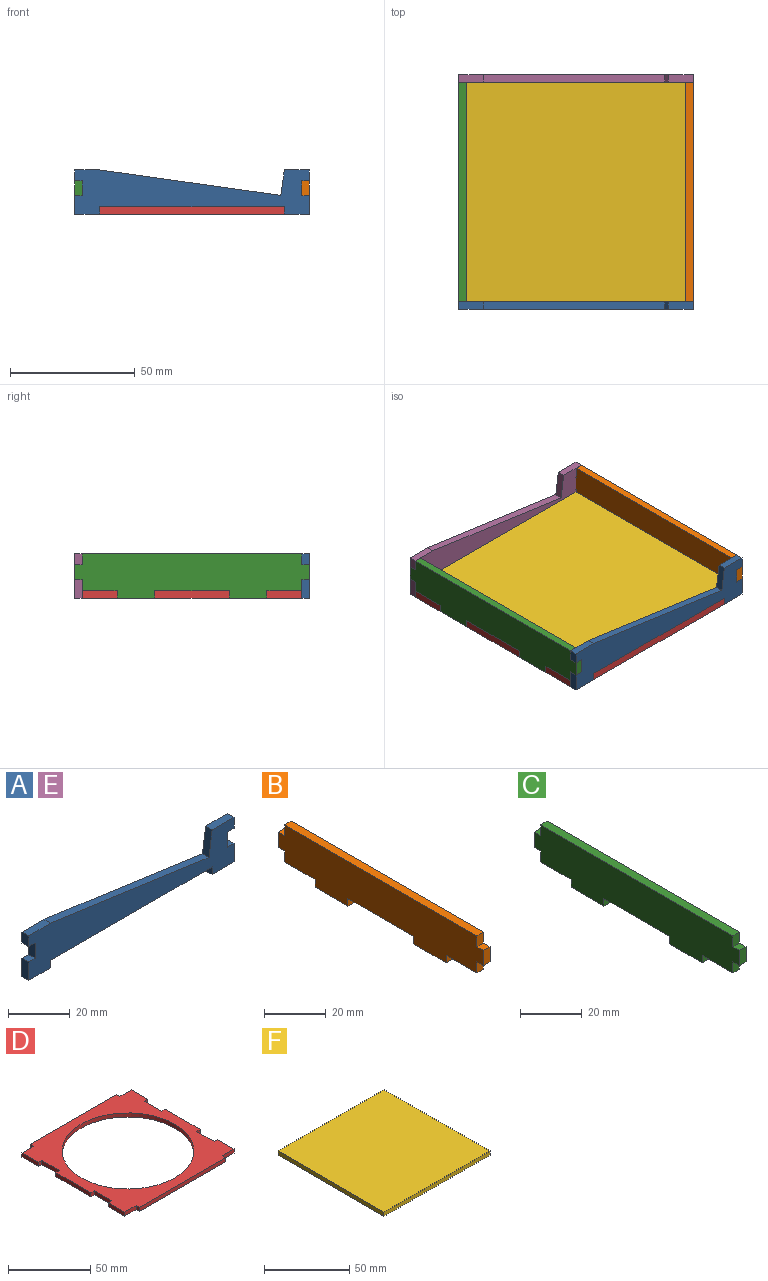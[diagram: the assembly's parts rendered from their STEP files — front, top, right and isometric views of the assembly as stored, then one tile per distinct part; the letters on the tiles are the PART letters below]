
ASSEMBLY  parts=6 mates=5
PART A: 21 faces, bbox 94x3x17.7 mm
  f0: plane 4.35x3mm, normal (1,0,0), area 13mm2, adj f2,f10,f14,f19
  f1: plane 7.35x3mm, normal (1,0,0), area 22mm2, adj f2,f9,f14,f20
  f2: plane 94x17.7mm, normal (0,-1,0), area 1028.3mm2, adj f0,f1,f3,f4,f5,f6,f7,f8
  f3: plane 7.35x3mm, normal (-1,0,0), area 22mm2, adj f2,f5,f14,f16
  f4: plane 4.35x3mm, normal (-1,0,0), area 13mm2, adj f2,f13,f14,f17
  f5: plane 10x3mm, normal (0,0,-1), area 30mm2, adj f2,f3,f6,f14
  f6: plane 3x3mm, normal (1,0,0), area 9mm2, adj f2,f5,f7,f14
  f7: plane 74x3mm, normal (0,0,-1), area 222mm2, adj f2,f6,f8,f14
  f8: plane 3x3mm, normal (-1,0,0), area 9mm2, adj f2,f7,f9,f14
  f9: plane 10x3mm, normal (0,0,-1), area 30mm2, adj f1,f2,f8,f14
  f10: plane 10x3mm, normal (0,0,1), area 30mm2, adj f0,f2,f11,f14
  f11: plane 10.2x3mm, normal (-0.99,0,0.14), area 30.9mm2, adj f2,f10,f12,f14
  f12: plane 72.57x10.2mm, normal (0.14,0,0.99), area 219.8mm2, adj f2,f11,f13,f14
  f13: plane 10x3mm, normal (0,0,1), area 30mm2, adj f2,f4,f12,f14
  f14: plane 94x17.7mm, normal (0,1,0), area 1028.3mm2, adj f0,f1,f3,f4,f5,f6,f7,f8
  f15: plane 6x3mm, normal (-1,0,0), area 18mm2, adj f2,f14,f16,f17
  f16: plane 3x3mm, normal (0,0,1), area 9mm2, adj f2,f3,f14,f15
  f17: plane 3x3mm, normal (0,0,-1), area 9mm2, adj f2,f4,f14,f15
  f18: plane 6x3mm, normal (1,0,0), area 18mm2, adj f2,f14,f19,f20
  f19: plane 3x3mm, normal (0,0,-1), area 9mm2, adj f0,f2,f14,f18
  f20: plane 3x3mm, normal (0,0,1), area 9mm2, adj f1,f2,f14,f18
PART B: 22 faces, bbox 3x94x17.7 mm
  f0: plane 3x3mm, normal (0,1,0), area 9mm2, adj f1,f19,f20,f21
  f1: plane 14x3mm, normal (0,0,-1), area 42mm2, adj f0,f2,f20,f21
  f2: plane 4.35x3mm, normal (0,1,0), area 13mm2, adj f1,f3,f20,f21
  f3: plane 3x3mm, normal (0,0,-1), area 9mm2, adj f2,f4,f20,f21
  f4: plane 6x3mm, normal (0,1,0), area 18mm2, adj f3,f5,f20,f21
  f5: plane 3x3mm, normal (0,0,1), area 9mm2, adj f4,f6,f20,f21
  f6: plane 4.35x3mm, normal (0,1,0), area 13mm2, adj f5,f7,f20,f21
  f7: plane 88x3mm, normal (0,0,1), area 264mm2, adj f6,f8,f20,f21
  f8: plane 4.35x3mm, normal (0,-1,0), area 13mm2, adj f7,f9,f20,f21
  f9: plane 3x3mm, normal (0,0,1), area 9mm2, adj f8,f10,f20,f21
  f10: plane 6x3mm, normal (0,-1,0), area 18mm2, adj f9,f11,f20,f21
  f11: plane 3x3mm, normal (0,0,-1), area 9mm2, adj f10,f12,f20,f21
  f12: plane 4.35x3mm, normal (0,-1,0), area 13mm2, adj f11,f13,f20,f21
  f13: plane 14x3mm, normal (0,0,-1), area 42mm2, adj f12,f14,f20,f21
  f14: plane 3x3mm, normal (0,-1,0), area 9mm2, adj f13,f15,f20,f21
  f15: plane 15x3mm, normal (0,0,-1), area 45mm2, adj f14,f16,f20,f21
  f16: plane 3x3mm, normal (0,1,0), area 9mm2, adj f15,f17,f20,f21
  f17: plane 30x3mm, normal (0,0,-1), area 90mm2, adj f16,f18,f20,f21
  f18: plane 3x3mm, normal (0,-1,0), area 9mm2, adj f17,f19,f20,f21
  f19: plane 15x3mm, normal (0,0,-1), area 45mm2, adj f0,f18,f20,f21
  f20: plane 94x17.7mm, normal (-1,0,0), area 1419.5mm2, adj f0,f1,f2,f3,f4,f5,f6,f7
  f21: plane 94x17.7mm, normal (1,0,0), area 1419.5mm2, adj f0,f1,f2,f3,f4,f5,f6,f7
PART C: 22 faces, bbox 3x94x17.7 mm
  f0: plane 3x3mm, normal (0,-1,0), area 9mm2, adj f1,f19,f20,f21
  f1: plane 30x3mm, normal (0,0,-1), area 90mm2, adj f0,f2,f20,f21
  f2: plane 3x3mm, normal (0,1,0), area 9mm2, adj f1,f3,f20,f21
  f3: plane 15x3mm, normal (0,0,-1), area 45mm2, adj f2,f4,f20,f21
  f4: plane 3x3mm, normal (0,-1,0), area 9mm2, adj f3,f5,f20,f21
  f5: plane 14x3mm, normal (0,0,-1), area 42mm2, adj f4,f6,f20,f21
  f6: plane 4.35x3mm, normal (0,-1,0), area 13mm2, adj f5,f7,f20,f21
  f7: plane 3x3mm, normal (0,0,-1), area 9mm2, adj f6,f8,f20,f21
  f8: plane 6x3mm, normal (0,-1,0), area 18mm2, adj f7,f9,f20,f21
  f9: plane 3x3mm, normal (0,0,1), area 9mm2, adj f8,f10,f20,f21
  f10: plane 4.35x3mm, normal (0,-1,0), area 13mm2, adj f9,f11,f20,f21
  f11: plane 88x3mm, normal (0,0,1), area 264mm2, adj f10,f12,f20,f21
  f12: plane 4.35x3mm, normal (0,1,0), area 13mm2, adj f11,f13,f20,f21
  f13: plane 3x3mm, normal (0,0,1), area 9mm2, adj f12,f14,f20,f21
  f14: plane 6x3mm, normal (0,1,0), area 18mm2, adj f13,f15,f20,f21
  f15: plane 3x3mm, normal (0,0,-1), area 9mm2, adj f14,f16,f20,f21
  f16: plane 4.35x3mm, normal (0,1,0), area 13mm2, adj f15,f17,f20,f21
  f17: plane 14x3mm, normal (0,0,-1), area 42mm2, adj f16,f18,f20,f21
  f18: plane 3x3mm, normal (0,1,0), area 9mm2, adj f17,f19,f20,f21
  f19: plane 15x3mm, normal (0,0,-1), area 45mm2, adj f0,f18,f20,f21
  f20: plane 94x17.7mm, normal (1,0,0), area 1419.5mm2, adj f0,f1,f2,f3,f4,f5,f6,f7
  f21: plane 94x17.7mm, normal (-1,0,0), area 1419.5mm2, adj f0,f1,f2,f3,f4,f5,f6,f7
PART D: 31 faces, bbox 94x94x3 mm
  f0: plane 14x3mm, normal (1,0,0), area 42mm2, adj f6,f10,f11,f26
  f1: plane 14x3mm, normal (1,0,0), area 42mm2, adj f6,f10,f15,f29
  f2: plane 30x3mm, normal (1,0,0), area 90mm2, adj f6,f10,f27,f30
  f3: plane 30x3mm, normal (-1,0,0), area 90mm2, adj f6,f10,f21,f23
  f4: plane 14x3mm, normal (-1,0,0), area 42mm2, adj f6,f10,f17,f20
  f5: plane 74x3mm, normal (0,1,0), area 222mm2, adj f6,f10,f12,f14
  f6: plane 94x94mm, normal (0,0,1), area 3509.5mm2, adj f0,f1,f2,f3,f4,f5,f7,f8
  f7: plane 74x3mm, normal (0,-1,0), area 222mm2, adj f6,f10,f16,f18
  f8: cylinder r=40mm len=80mm, axis (0,0,-1), area 754mm2, adj f6,f10
  f9: plane 14x3mm, normal (-1,0,0), area 42mm2, adj f6,f10,f13,f24
  f10: plane 94x94mm, normal (0,0,-1), area 3509.5mm2, adj f0,f1,f2,f3,f4,f5,f7,f8
  f11: plane 10x3mm, normal (0,1,0), area 30mm2, adj f0,f6,f10,f12
  f12: plane 3x3mm, normal (1,0,0), area 9mm2, adj f5,f6,f10,f11
  f13: plane 10x3mm, normal (0,1,0), area 30mm2, adj f6,f9,f10,f14
  f14: plane 3x3mm, normal (-1,0,0), area 9mm2, adj f5,f6,f10,f13
  f15: plane 10x3mm, normal (0,-1,0), area 30mm2, adj f1,f6,f10,f16
  f16: plane 3x3mm, normal (1,0,0), area 9mm2, adj f6,f7,f10,f15
  f17: plane 10x3mm, normal (0,-1,0), area 30mm2, adj f4,f6,f10,f18
  f18: plane 3x3mm, normal (-1,0,0), area 9mm2, adj f6,f7,f10,f17
  f19: plane 15x3mm, normal (-1,0,0), area 45mm2, adj f6,f10,f20,f21
  f20: plane 3x3mm, normal (0,1,0), area 9mm2, adj f4,f6,f10,f19
  f21: plane 3x3mm, normal (0,-1,0), area 9mm2, adj f3,f6,f10,f19
  f22: plane 15x3mm, normal (-1,0,0), area 45mm2, adj f6,f10,f23,f24
  f23: plane 3x3mm, normal (0,1,0), area 9mm2, adj f3,f6,f10,f22
  f24: plane 3x3mm, normal (0,-1,0), area 9mm2, adj f6,f9,f10,f22
  f25: plane 15x3mm, normal (1,0,0), area 45mm2, adj f6,f10,f26,f27
  f26: plane 3x3mm, normal (0,-1,0), area 9mm2, adj f0,f6,f10,f25
  f27: plane 3x3mm, normal (0,1,0), area 9mm2, adj f2,f6,f10,f25
  f28: plane 15x3mm, normal (1,0,0), area 45mm2, adj f6,f10,f29,f30
  f29: plane 3x3mm, normal (0,1,0), area 9mm2, adj f1,f6,f10,f28
  f30: plane 3x3mm, normal (0,-1,0), area 9mm2, adj f2,f6,f10,f28
PART E: same geometry as A
PART F: 6 faces, bbox 88x88x3 mm
  f0: plane 88x3mm, normal (0,1,0), area 264mm2, adj f1,f3,f4,f5
  f1: plane 88x3mm, normal (-1,0,0), area 264mm2, adj f0,f2,f4,f5
  f2: plane 88x3mm, normal (0,-1,0), area 264mm2, adj f1,f3,f4,f5
  f3: plane 88x3mm, normal (1,0,0), area 264mm2, adj f0,f2,f4,f5
  f4: plane 88x88mm, normal (0,0,1), area 7744mm2, adj f0,f1,f2,f3
  f5: plane 88x88mm, normal (0,0,-1), area 7744mm2, adj f0,f1,f2,f3
PLACE A t=(13.14,-20.77,11.05)mm
PLACE B t=(13.14,-20.77,11.05)mm
PLACE C t=(13.14,-20.77,11.05)mm
PLACE D t=(13.14,-20.77,11.05)mm fixed
PLACE E t=(13.14,70.23,11.05)mm
PLACE F t=(13.14,-20.77,11.05)mm
MATE fastened A.f20 <-> B.f11  axis (0,0,1) through (58.64,-66.27,18.4)mm
MATE fastened A.f17 <-> C.f9  axis (0,0,-1) through (-32.36,-66.27,24.4)mm
MATE fastened A.f14 <-> D.f17  axis (0,1,0) through (-28.86,-64.77,12.55)mm
MATE fastened E.f2 <-> D.f13  axis (0,-1,0) through (-28.86,23.23,12.55)mm
MATE fastened F.f5 <-> D.f8  axis (0,0,-1) through (13.14,-20.77,14.05)mm
